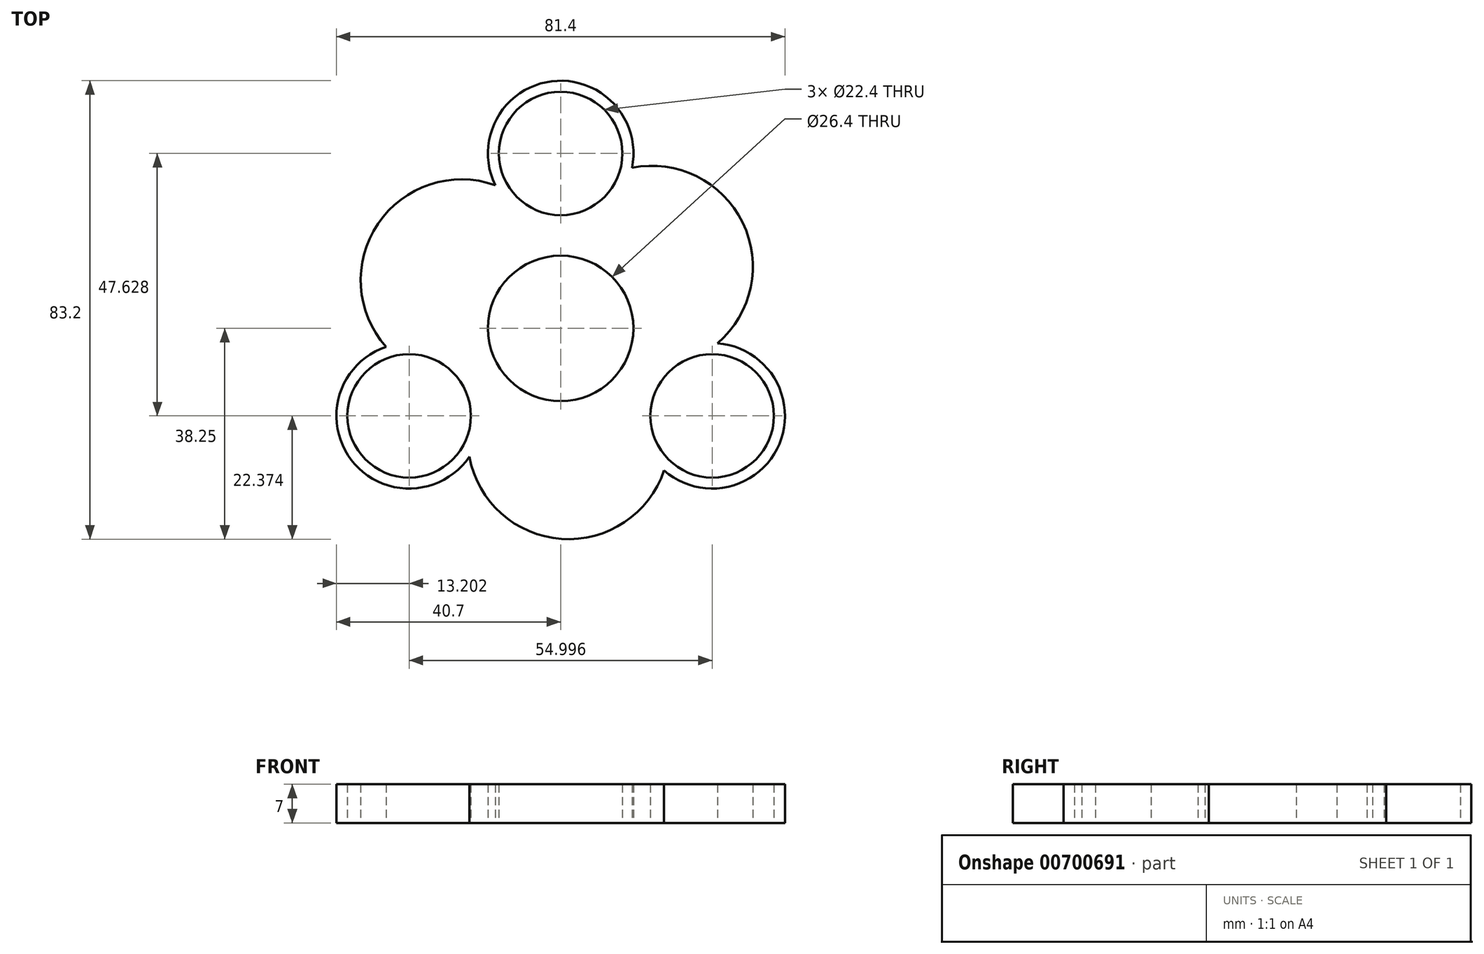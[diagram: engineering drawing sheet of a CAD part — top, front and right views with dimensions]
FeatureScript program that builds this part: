
annotation { "Feature Type Name" : "Feature", "Feature Type Description" : "" }
export const myFeature = defineFeature(function(context is Context, id is Id, definition is map)
    precondition{}
    {
        {
            var Q0;
            Q0=qCreatedBy(makeId("Top.planeOp"),FACE);
            var sketch = newSketch(context, id + "F0", { "sketchPlane" : qUnion([Q0])});
            skCircle(sketch, "E0", {"center": v(0, 0) * mm, "radius": 11.2 * mm});
            skCircle(sketch, "E1", {"center": v(0, 0) * mm, "radius": 13.2 * mm});
            skCircle(sketch, "E2", {"center": v(0, 31.75) * mm, "radius": 11.2 * mm});
            skArc(sketch, "E3", {"start": v(12.94, 29.14) * mm, "mid": v(-1.66, 44.85) * mm, "end": v(-11.88, 26) * mm});
            skArc(sketch, "E4.1.0", {"start": v(-31.7, -3.36) * mm, "mid": v(-38.01, -23.86) * mm, "end": v(-16.58, -23.29) * mm});
            skCircle(sketch, "E4.1.1", {"center": v(-27.5, -15.88) * mm, "radius": 11.2 * mm});
            skArc(sketch, "E4.2.0", {"start": v(18.77, -25.78) * mm, "mid": v(39.67, -20.99) * mm, "end": v(28.45, -2.71) * mm});
            skCircle(sketch, "E4.2.1", {"center": v(27.5, -15.88) * mm, "radius": 11.2 * mm});
            skArc(sketch, "E5", {"start": v(-11.88, 26) * mm, "mid": v(-33.15, 18.99) * mm, "end": v(-31.7, -3.36) * mm});
            skArc(sketch, "E6.1.0", {"start": v(-16.58, -23.29) * mm, "mid": v(0.13, -38.2) * mm, "end": v(18.77, -25.78) * mm});
            skArc(sketch, "E6.2.0", {"start": v(28.45, -2.71) * mm, "mid": v(33.02, 19.22) * mm, "end": v(12.94, 29.14) * mm});
            skSolve(sketch);
        }
        {
            var Q0;
            Q0=makeQuery(id+"F0.imprint","IMPRINT",FACE,{"disambiguationData":[TD([[makeQuery(id+"F0.imprint","IMPRINT",EDGE,{"derivedFrom":sQuery(id+"F0.wireOp",EDGE,"E1")}),-1.0]])]});
            extrude(context, id + "F1", {"entities" : qUnion([Q0]), "depth" : 7 * mm, "offsetDistance" : 25 * mm});
        }
    });
